# Revit family: LTR-3RD
name_source: partatom
category: Lighting Fixtures
units: mm (PartAtom-declared; Revit-internal decimal feet)

## family parameters
Cut with Voids When Loaded = No
Host = Face
Light Source = Yes
OmniClass Number = 23.80.70.11.14.11
OmniClass Title = Downlights
Part Type = Normal
Room Calculation Point = No
Round Connector Dimension = Use Diameter
Shared = Yes

## types (1)
- Liteistry-3
    Apparent Load = 0 VA
    Assembly Code = D5020200
    Color Filter = 16777215
    Default Elevation = 48 "
    Description = 3in LED Downlight
    Dimming Lamp Color Temperature Shift = <None>
    Emit Shape Visible in Rendering = No
    Emit from Circle Diameter = 3 "
    Features = 3inch architectural LED downlight delivering 600–2000 lm
• Four beam distributions from 0.4 to 1.1 Spacing Criteria
• Quiet reflector appearance with 50º optical cutoff
• 2700K–5000K, 80+ and 90+ CRI options
• Available for New Construction (non-IC), Remodel (non-IC), IC
and Chicago Plenum applications
• Variety of dimming protocol options including 0-10V, DALI, DMX,
Lutron Forward Phase and EcoSystem
• NX Distributed Intelligence™ wired and wireless controls
capability available
    Glass = White Glass
    Hardware Finish = Steel
    Lamp = LED
    Load Classification = Lighting
    Manufacturer = Prescolite
    Model = LTR-3RD
    Photometric Notes = More IES files download on Photometric Web Link
    Photometric Web File = LTR-3RD-H-ML20L-DM1 LTR-3RD-T-ML35K8MDS.ies
    Power Factor = 1
    Tilt Angle = -90.00°
    URL = https://www.currentlighting.com
    Voltage = 120 V
    Warranty = 5Years limited warranty
    Wattage Comments = 13.4, 17.8 & 22.2

## geometry (parser evidence)
native form markers: Blend x5, Sweep x1
no freeform markers — native parametric forms only
